# Revit family: VLN_Nim-II-Mes-E_F3072_BIM_NL
name_source: partatom
category: Plumbing Fixtures
revit_build: Autodesk Revit MEP 2014 (Build: 20130308_1515(x64)
units: mm (PartAtom-declared; Revit-internal decimal feet)

## types (1)
- F3072AA - NIM-II-MES-E DOUCHE M KR OPBOUW CHR
    Accessories = www.idealstandardnederland.nl
    AreaUnits = millimeters
    Assembly Code = C1030200
    AssetType = Vast
    BIMObjectName = VLN_Venlo_ShowerManualWaterSupplySets_F3072AA
    BREEAMApproved = No
    BarCode = 8711678063106
    Brand = Venlo
    CWFU = 0
    CodePerformance = EN 817, DIN 4109
    Color = Chroom
    ConnectionType = Sanitair
    Cost = 0 $
    Default Elevation = 800 mm  [stored 2.62467 ft]
    Description = Venlo Nimbus II Messing doucheblokmengkraan eco. H.o.h. 63,5 mm. Omstelling. Koppeling 12 mm. Aansluiting G1/2". Eco bovendelen. Zonder uitloop.
    DurationUnit = jaar
    ECA = No
    ExpectedLife = 25
    FaucetFunction = Mengkraan
    FaucetOperation = Tweegreeps
    FaucetType = Doucheblokmengkraan
    Features = Doucheblokmengkraan eco. H.o.h. 63,5 mm. Omstelling. Koppeling 12 mm. Aansluiting G1/2". Eco bovendelen. Zonder uitloop.
    Finish = Chroom
    HWFU = 0
    IfcExportAs = IfcValveType
    IfcExportType = FAUCET
    InstallationInstructions = http://www.idealstandardnederland.nl
    LinearUnits = millimeters
    ManufacturerURL = www.idealstandardnederland.nl
    Material = Messing
    Model = F3072AA
    ModelNumber = F3072AA
    ModelReference = Venlo Nimbus II Messing doucheblokmengkraan eco. H.o.h. 63,5 mm. Omstelling. Koppeling 12 mm. Aansluiting G1/2". Eco bovendelen. Zonder uitloop.
    NBSDescription = Shower mixers
    NBSReference = 45-35-70/335
    Name = ShowerManualWaterSupplySets_F3072AA_Venlo
    NettWeight = 1.33 kg
    NominalHeight = 74 mm
    NominalLength = 85 mm  [stored 0.278871 ft]
    NominalWidth = 204 mm
    ProductInformation = http://www.idealstandardnederland.nl
    Shape = Gesculptuurd
    Size = 204 x 85 x 74 mm
    Space = Internal
    SpareParts = www.idealstandardnederland.nl
    TMV3 = Yes
    TestPressure = 10 Bar
    URL = www.idealstandardnederland.nl
    Uniclass2015Code = Pr_40_20_87_78
    Uniclass2015Title = Shower manual water supply sets
    Uniclass2015Version = Products v1.1
    ValveMechanism = Keramische schijven
    ValveOperation = Tweegreeps
    Version = 1
    VolumeUnits = liter
    WFU = 0
    WRAS = No
    WarrantyDescription = Fabrieksgarantie
    WarrantyDurationParts = 10
    WarrantyDurationUnit = jaar
    WaterEfficientProduct = No
    WorkingPressure = 1-5 bar

note: [stored X ft] marks values corroborated as IEEE doubles in the binary element streams (Revit-internal decimal feet)

## geometry (parser evidence)
native form markers: Sweep x1
no freeform markers — native parametric forms only
